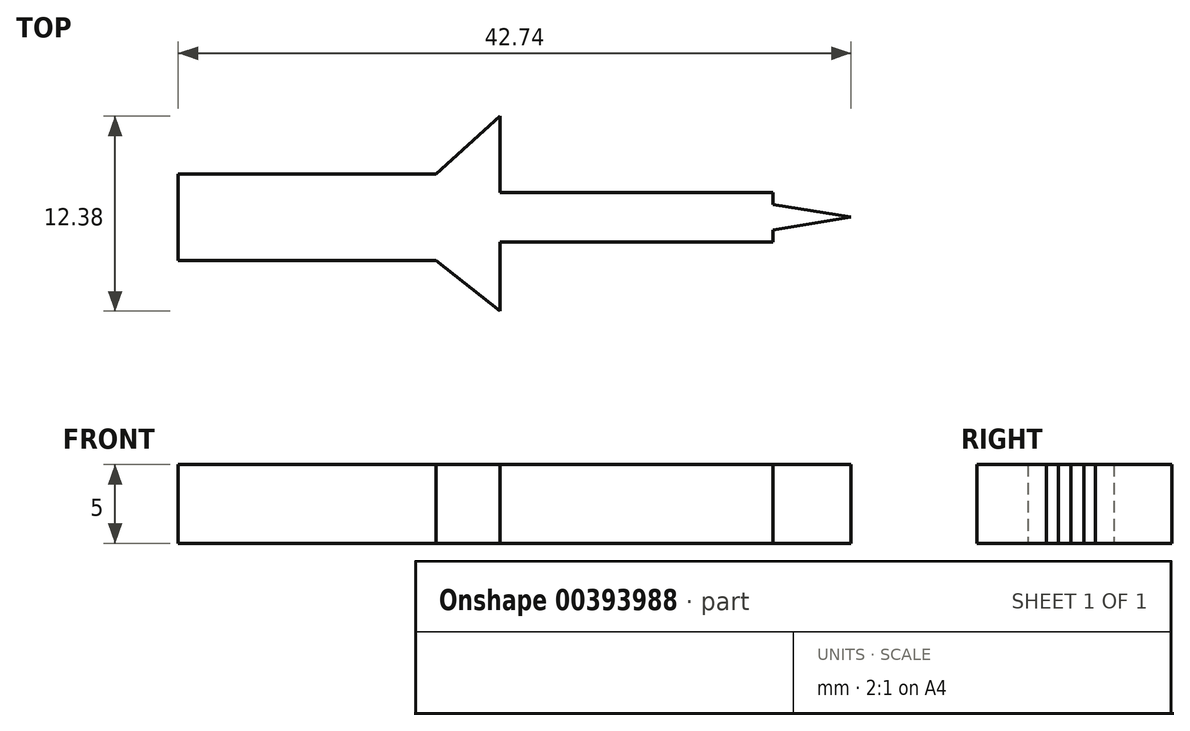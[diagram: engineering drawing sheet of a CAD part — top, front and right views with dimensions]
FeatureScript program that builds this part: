
annotation { "Feature Type Name" : "Feature", "Feature Type Description" : "" }
export const myFeature = defineFeature(function(context is Context, id is Id, definition is map)
    precondition{}
    {
        {
            var Q0;
            Q0=qCreatedBy(makeId("Top.planeOp"),FACE);
            var sketch = newSketch(context, id + "F0", { "sketchPlane" : qUnion([Q0])});
            skLineSegment(sketch, "E0.bottom", {"start": v(0, 0) * mm, "end": v(150, 0) * mm});
            skLineSegment(sketch, "E0.top", {"start": v(0, -150) * mm, "end": v(150, -150) * mm});
            skLineSegment(sketch, "E0.left", {"start": v(0, 0) * mm, "end": v(0, -150) * mm});
            skLineSegment(sketch, "E0.right", {"start": v(150, 0) * mm, "end": v(150, -150) * mm});
            skLineSegment(sketch, "E1", {"start": v(75, 0) * mm, "end": v(75, -150) * mm, "construction": true});
            skSolve(sketch);
        }
        {
            var Q0;
            Q0=makeQuery(id+"F0.imprint","IMPRINT",FACE,{"disambiguationData":[TD([[makeQuery(id+"F0.imprint","IMPRINT",EDGE,{"derivedFrom":sQuery(id+"F0.wireOp",EDGE,"E0.bottom")}),-1.0]])]});
            var sketch = newSketch(context, id + "F1", { "sketchPlane" : qUnion([Q0])});
            skLineSegment(sketch, "E2.bottom", {"start": v(60.81, -96.89) * mm, "end": v(44.44, -96.89) * mm});
            skLineSegment(sketch, "E2.top", {"start": v(60.81, -91.41) * mm, "end": v(44.44, -91.41) * mm});
            skLineSegment(sketch, "E2.left", {"start": v(60.81, -96.89) * mm, "end": v(60.81, -91.41) * mm});
            skLineSegment(sketch, "E2.right", {"start": v(44.44, -96.89) * mm, "end": v(44.44, -91.41) * mm});
            skLineSegment(sketch, "E3", {"start": v(64.87, -87.73) * mm, "end": v(64.87, -94.15) * mm});
            skLineSegment(sketch, "E4", {"start": v(64.87, -94.15) * mm, "end": v(64.87, -100.1) * mm});
            skLineSegment(sketch, "E5", {"start": v(60.81, -96.89) * mm, "end": v(64.87, -100.1) * mm});
            skLineSegment(sketch, "E6", {"start": v(60.81, -91.41) * mm, "end": v(64.87, -87.73) * mm});
            skLineSegment(sketch, "E7.bottom", {"start": v(82.2, -95.7) * mm, "end": v(64.87, -95.7) * mm});
            skLineSegment(sketch, "E7.top", {"start": v(82.2, -92.59) * mm, "end": v(64.87, -92.59) * mm});
            skLineSegment(sketch, "E7.left", {"start": v(82.2, -95.7) * mm, "end": v(82.2, -92.59) * mm});
            skPoint(sketch, "E7.middle", {"position": v(64.87, -94.15) * mm});
            skPoint(sketch, "E7.right.end.orphan", {"position": v(47.54, -92.59) * mm});
            skPoint(sketch, "E7.right.start.orphan", {"position": v(47.54, -95.7) * mm});
            skLineSegment(sketch, "E8", {"start": v(82.2, -94.96) * mm, "end": v(87.18, -94.15) * mm});
            skLineSegment(sketch, "E9.MirrorCS", {"start": v(82.2, -93.34) * mm, "end": v(87.18, -94.15) * mm});
            skPoint(sketch, "E10.start.orphan", {"position": v(82.2, -94.15) * mm});
            skSolve(sketch);
        }
        {
            var Q0;
            Q0 = qSketchRegion(id + "F1", true);
            var Q1;
            Q1=makeQuery(id+"F1.imprint","IMPRINT",FACE,{"disambiguationData":[TD([[makeQuery(id+"F1.imprint","IMPRINT",EDGE,{"derivedFrom":sQuery(id+"F1.wireOp",EDGE,"E2.left")}),-1.0]])]});
            var Q2;
            {var subQ4=sQuery(id+"F1.wireOp",EDGE,"E7.bottom");Q2=makeQuery(id+"F1.imprint","IMPRINT",FACE,{"disambiguationData":[TD([[makeQuery(id+"F1.imprint","IMPRINT",EDGE,{"derivedFrom":subQ4}),-1.0]])]});}
            var Q3;
            Q3=makeQuery(id+"F1.imprint","IMPRINT",FACE,{"disambiguationData":[TD([[makeQuery(id+"F1.imprint","IMPRINT",EDGE,{"derivedFrom":sQuery(id+"F1.wireOp",EDGE,"E2.bottom")}),-1.0]])]});
            var Q4;
            {var subQ0=sQuery(id+"F1.wireOp",EDGE,"E8");Q4=makeQuery(id+"F1.imprint","IMPRINT",FACE,{"disambiguationData":[TD([[makeQuery(id+"F1.imprint","IMPRINT",EDGE,{"derivedFrom":subQ0}),1.0]])]});}
            extrude(context, id + "F2", {"entities" : qUnion([Q0, Q1, Q2, Q3, Q4]), "depth" : 5 * mm});
        }
    });
